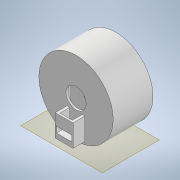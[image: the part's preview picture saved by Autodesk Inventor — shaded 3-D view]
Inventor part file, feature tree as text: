
AUTODESK INVENTOR PART (.ipt)
format: ipt  version: 2022.2 (Build 262287000, 287)  size: 298,496 bytes
history: native  units: mm
features: sketch x8, extrude x7, other x4, reference x4, projected_geometry x3, hole x2, plane x1
ambient origin geometry x8: Origin, YZ Plane, XZ Plane, XY Plane, X Axis, Y Axis, Z Axis, Center Point
bodies: Solid1 (feature_tree)
feature tree (29):
  other  "Motor.ipt"
  extrude  "Extrusion1"  Depth=4.0mm
  extrude  "Extrusion2"  TaperAngle=0.0deg  [1 undecoded]
  extrude  "Extrusion8"  Depth=10.0mm
  extrude  "Extrusion9"  Depth=2.0mm
  extrude  "Extrusion10"  Depth=2.4mm
  plane  "Work Plane6"
  hole  "Hole2"  [1 undecoded]
  hole  "Hole3"  [1 undecoded]
  extrude  "Extrusion11"  Depth=5.1mm
  extrude  "Extrusion12"  Depth=0.5mm
  reference  "Reference1"
  reference  "Reference2"
  sketch  "Sketch2"  dims[d0=4.0mm d1=7.0mm d6=3.2mm]
  reference  "Reference4"
  reference  "Reference5"
  projected_geometry  "Projected Loop11"
  sketch  "Sketch11"  dims[d8=0.0mm d15=0.0mm]
  sketch  "Sketch12"  dims[d35=10.0mm d51=0.3mm]
  sketch  "Sketch13"  dims[d53=2.0mm d55=2.5mm]
  sketch  "Sketch14"  dims[d57=6.2mm d58=2.4mm]
  projected_geometry  "Projected Loop14"
  sketch  "Sketch15"  dims[d59=1.0mm d60=0.0mm d61=8.16mm]
  sketch  "Sketch16"  dims[d62=5.1mm d63=0.0mm d64=8.16mm]
  sketch  "Sketch17"  dims[d65=10.0mm d66=0.0mm d67=5.1mm d68=2.04mm d69=5.8mm d70=2.6mm d71=3.2mm d72=6.0mm d73=6.0mm d74=3.0mm d75=90.0deg d76=8.0mm d77=0.0mm d78=3.2mm d79=6.0mm d80=6.0mm d81=2.0mm d82=90.0deg d83=8.0mm d84=0.0mm d85=9.0mm d86=5.25mm d87=0.25mm d88=0.0mm d89=0.0mm d90=2.0mm d91=13.4mm d93=0.6mm d94=0.0mm d28=0.5mm d29=0.872665mm d30=0.5mm d31=0.872665mm d49=0.5mm d50=0.872665mm d52=0.872665mm]
  projected_geometry  "Projected Loop16"
  other  "<userpath>\Documents\Inventor\Wire Bender\Assembly.iam"
  other  "Assembly.iam"
  other  "Tool Head:1"
note: 3 required parameter values undecoded (feature->parameter linkage not recoverable at this tier; creation-order binding heuristic only, values carry confidence <= 0.55)
